FCSTD DOCUMENT  (FreeCAD 0.19R)
Label: cebelnjak
License: All rights reserved
LicenseURL: http://en.wikipedia.org/wiki/All_rights_reserved
objects: App::Link×5, App::DocumentObjectGroup×3, PartDesign::CoordinateSystem×1, App::FeaturePython×1, App::Part×1, TechDraw::DrawSVGTemplate×1, TechDraw::DrawViewPart×1, TechDraw::DrawPage×1
note: 1 computed .brp shape members not serialized (recipe doc carries the construction recipe); baked Part::Feature solids carry a one-line shape summary decoded from their .brp
EXTERNAL_REF file=podstavek.FCStd obj=LCS_Origin
EXTERNAL_REF file=podstavek.FCStd obj=Assembly
EXTERNAL_REF file=panj.FCStd obj=LCS_Origin
EXTERNAL_REF file=podstavek.FCStd obj=LCS_panj1
EXTERNAL_REF file=panj.FCStd obj=Assembly
EXTERNAL_REF file=podstavek.FCStd obj=LCS_panj2
EXTERNAL_REF file=podstavek.FCStd obj=LCS_panj3
EXTERNAL_REF file=podstavek.FCStd obj=LCS_panj4

FEATURE [App::DocumentObjectGroup] Parts
FEATURE [PartDesign::CoordinateSystem] LCS_Origin
  AttacherType = Attacher::AttachEngine3D
  MapMode = 2
  Support = -> [X_Axis]
FEATURE [App::FeaturePython] Variables  # WARN: FeaturePython — macro-defined, semantics opaque (R4)
  Type = App::PropertyContainer
FEATURE [App::DocumentObjectGroup] Constraints
FEATURE [App::DocumentObjectGroup] Configurations
FEATURE [App::Link] podstavek
  AttachedBy = #LCS_Origin
  AttachedTo = Parent Assembly#LCS_Origin
  LinkedObject = -> <external podstavek.FCStd>#Assembly
  SolverId = Asm4EE
  expr: Placement = LCS_Origin.Placement * AttachmentOffset * podstavek#LCS_Origin.Placement ^ -1
FEATURE [App::Link] panj  label="panj_1"
  AttachedBy = #LCS_Origin
  AttachedTo = podstavek#LCS_panj1
  LinkPlacement = pos=(-900,0,500) rot=(0,0,1;0rad)
  LinkedObject = -> <external panj.FCStd>#Assembly
  Placement = pos=(-900,0,500) rot=(0,0,1;0rad)
  SolverId = Asm4EE
  expr: Placement = podstavek.Placement * podstavek#LCS_panj1.Placement * AttachmentOffset * panj#LCS_Origin.Placement ^ -1
FEATURE [App::Link] panj_2
  AttachedBy = #LCS_Origin
  AttachedTo = podstavek#LCS_panj2
  LinkPlacement = pos=(-300,0,500) rot=(0,0,1;0rad)
  LinkedObject = -> <external panj.FCStd>#Assembly
  Placement = pos=(-300,0,500) rot=(0,0,1;0rad)
  SolverId = Asm4EE
  expr: Placement = podstavek.Placement * podstavek#LCS_panj2.Placement * AttachmentOffset * panj#LCS_Origin.Placement ^ -1
FEATURE [App::Link] panj_3
  AttachedBy = #LCS_Origin
  AttachedTo = podstavek#LCS_panj3
  LinkPlacement = pos=(300,0,500) rot=(0,0,1;0rad)
  LinkedObject = -> <external panj.FCStd>#Assembly
  Placement = pos=(300,0,500) rot=(0,0,1;0rad)
  SolverId = Asm4EE
  expr: Placement = podstavek.Placement * podstavek#LCS_panj3.Placement * AttachmentOffset * panj#LCS_Origin.Placement ^ -1
FEATURE [App::Link] panj_4
  AttachedBy = #LCS_Origin
  AttachedTo = podstavek#LCS_panj4
  LinkPlacement = pos=(900,0,500) rot=(0,0,1;0rad)
  LinkedObject = -> <external panj.FCStd>#Assembly
  Placement = pos=(900,0,500) rot=(0,0,1;0rad)
  SolverId = Asm4EE
  expr: Placement = podstavek.Placement * podstavek#LCS_panj4.Placement * AttachmentOffset * panj#LCS_Origin.Placement ^ -1
FEATURE [App::Part] Assembly
  AssemblyType = Part::Link
  Group = -> [LCS_Origin,Variables,Constraints,Configurations,podstavek,panj,panj_2,panj_3,panj_4]
  Origin = -> Origin
  Type = Assembly
FEATURE [TechDraw::DrawSVGTemplate] Template
  EditableTexts = AVTOR=Brane Borštnik; AVTOR_2=Risal: Janez Paternoster; DATUM=6.5.2022; MERILO=1:10; NAZIV=Dadant-Blatt panji; STRAN=Stran 1/1; VIR=https://github.com/<owner>/Dadant-Blatt
  Height = 210
  Orientation = 1
  Width = 297
FEATURE [TechDraw::DrawViewPart] View
  CoarseView = false
  Direction = (0.333,-0.882,0.333)
  Focus = 100
  HardHidden = false
  IsoCount = 0
  IsoHidden = false
  IsoVisible = false
  LockPosition = false
  Perspective = false
  Rotation = 0
  Scale = 0.09
  ScaleType = 0
  SeamHidden = false
  SeamVisible = true
  SmoothHidden = false
  SmoothVisible = true
  Source = -> [Assembly]
  X = 148.5
  XDirection = (0.935,0.354,0)
  Y = 105
FEATURE [TechDraw::DrawPage] Page
  KeepUpdated = true
  NextBalloonIndex = 1
  ProjectionType = 0
  Scale = 0.09
  Template = -> Template
  Views = -> [View]

RESOLVED EXTERNAL PARTS (link-assembly join: the EXTERNAL_REF files above that resolve inside this repo's crawl, each included once):
---- part panj.FCStd = doc fcstd_6ccb10f4a623 ----
FCSTD DOCUMENT  (FreeCAD 0.19R)
Label: panj
License: All rights reserved
LicenseURL: http://en.wikipedia.org/wiki/All_rights_reserved
objects: App::Link×9, PartDesign::CoordinateSystem×4, App::DocumentObjectGroup×3, TechDraw::DrawSVGTemplate×3, TechDraw::DrawViewPart×3, TechDraw::DrawPage×3, App::Part×2, TechDraw::DrawViewSection×2, App::FeaturePython×1, Sketcher::SketchObject×1, PartDesign::Pad×1, PartDesign::Body×1
note: 8 computed .brp shape members not serialized (recipe doc carries the construction recipe); baked Part::Feature solids carry a one-line shape summary decoded from their .brp
EXTERNAL_REF file=podnica_ohisje.FCStd obj=LCS_bottom
EXTERNAL_REF file=podnica_ohisje.FCStd obj=Assembly
EXTERNAL_REF file=podnica_ohisje.FCStd obj=LCS_insert_low
EXTERNAL_REF file=smukalnik.FCStd obj=LCS_podnica
EXTERNAL_REF file=smukalnik.FCStd obj=Assembly
EXTERNAL_REF file=podnica_ohisje.FCStd obj=LCS_insert
EXTERNAL_REF file=smukalnik_mreza.FCStd obj=LCS_spreaj
EXTERNAL_REF file=smukalnik_mreza.FCStd obj=Assembly
EXTERNAL_REF file=podnica_ohisje.FCStd obj=LCS_pokrovcek
EXTERNAL_REF file=podnica_pokrovcek.FCStd obj=LCS_Origin
EXTERNAL_REF file=podnica_pokrovcek.FCStd obj=Assembly
EXTERNAL_REF file=naklada.FCStd obj=LCS_Origin
EXTERNAL_REF file=podnica_ohisje.FCStd obj=LCS_Origin
EXTERNAL_REF file=naklada.FCStd obj=Assembly
EXTERNAL_REF file=naklada.FCStd obj=LCS_1
EXTERNAL_REF file=naklada_nizka.FCStd obj=LCS_Origin
EXTERNAL_REF file=naklada_nizka.FCStd obj=Assembly
EXTERNAL_REF file=naklada_nizka.FCStd obj=LCS_1
EXTERNAL_REF file=pokrov.FCStd obj=LCS_botton
EXTERNAL_REF file=pokrov.FCStd obj=Assembly
EXTERNAL_REF file=pokrov.FCStd obj=LCS_1
EXTERNAL_REF file=streha.FCStd obj=LCS_Origin
EXTERNAL_REF file=streha.FCStd obj=Assembly

FEATURE [PartDesign::CoordinateSystem] LCS_Origin
  AttacherType = Attacher::AttachEngine3D
  MapMode = 2
  Support = -> [X_Axis]
FEATURE [App::FeaturePython] Variables  # WARN: FeaturePython — macro-defined, semantics opaque (R4)
  Type = App::PropertyContainer
FEATURE [App::DocumentObjectGroup] Constraints
FEATURE [App::DocumentObjectGroup] Configurations
FEATURE [App::Link] podnica_ohisje
  AttachedBy = #LCS_bottom
  AttachedTo = Parent Assembly#LCS_Origin
  LinkPlacement = pos=(0,0,120) rot=(0,0,1;0rad)
  LinkedObject = -> <external podnica_ohisje.FCStd>#Assembly
  Placement = pos=(0,0,120) rot=(0,0,1;0rad)
  SolverId = Asm4EE
  expr: Placement = LCS_Origin.Placement * AttachmentOffset * podnica_ohisje#LCS_bottom.Placement ^ -1
FEATURE [App::Link] smukalnik
  AttachedBy = #LCS_podnica
  AttachedTo = podnica_ohisje#LCS_insert_low
  LinkPlacement = pos=(0,-234,65) rot=(0,0,1;0rad)
  LinkedObject = -> <external smukalnik.FCStd>#Assembly
  Placement = pos=(0,-234,65) rot=(0,0,1;0rad)
  SolverId = Asm4EE
  expr: Placement = podnica_ohisje.Placement * podnica_ohisje#LCS_insert_low.Placement * AttachmentOffset * smukalnik#LCS_podnica.Placement ^ -1
FEATURE [App::Link] smukalnik_mreza
  AttachedBy = #LCS_spreaj
  AttachedTo = podnica_ohisje#LCS_insert
  LinkPlacement = pos=(0,18.5,35) rot=(0,0,1;0rad)
  LinkedObject = -> <external smukalnik_mreza.FCStd>#Assembly
  Placement = pos=(0,18.5,35) rot=(0,0,1;0rad)
  SolverId = Asm4EE
  expr: Placement = podnica_ohisje.Placement * podnica_ohisje#LCS_insert.Placement * AttachmentOffset * smukalnik_mreza#LCS_spreaj.Placement ^ -1
FEATURE [App::Link] podnica_pokrovcek
  AttachedBy = #LCS_Origin
  AttachedTo = podnica_ohisje#LCS_pokrovcek
  LinkPlacement = pos=(0,-252,35) rot=(0,0,1;0rad)
  LinkedObject = -> <external podnica_pokrovcek.FCStd>#Assembly
  Placement = pos=(0,-252,35) rot=(0,0,1;0rad)
  SolverId = Asm4EE
  expr: Placement = podnica_ohisje.Placement * podnica_ohisje#LCS_pokrovcek.Placement * AttachmentOffset * podnica_pokrovcek#LCS_Origin.Placement ^ -1
FEATURE [App::Link] naklada
  AttachedBy = #LCS_Origin
  AttachedTo = podnica_ohisje#LCS_Origin
  LinkPlacement = pos=(0,0,120) rot=(0,0,1;0rad)
  LinkedObject = -> <external naklada.FCStd>#Assembly
  Placement = pos=(0,0,120) rot=(0,0,1;0rad)
  SolverId = Asm4EE
  expr: Placement = podnica_ohisje.Placement * podnica_ohisje#LCS_Origin.Placement * AttachmentOffset * naklada#LCS_Origin.Placement ^ -1
FEATURE [PartDesign::CoordinateSystem] LCS_0  label="LCS_bottom"
  AttacherType = Attacher::AttachEngine3D
  MapMode = 2
  Support = -> [X_Axis001]
FEATURE [PartDesign::CoordinateSystem] LCS_0001
  AttacherType = Attacher::AttachEngine3D
  MapMode = 2
  Support = -> [X_Axis002]
FEATURE [Sketcher::SketchObject] Sketch
  FullyConstrained = true
  MapMode = 5
  Support = -> [XY_Plane002]
  sketch-geometry (4):
    g0: LineSegment StartX=-214 StartY=-249.5 StartZ=0 EndX=214 EndY=-249.5 EndZ=0
    g1: LineSegment StartX=214 StartY=-249.5 StartZ=0 EndX=214 EndY=249.5 EndZ=0
    g2: LineSegment StartX=214 StartY=249.5 StartZ=0 EndX=-214 EndY=249.5 EndZ=0
    g3: LineSegment StartX=-214 StartY=249.5 StartZ=0 EndX=-214 EndY=-249.5 EndZ=0
  constraints (10):
    c: Coincident(g0,g1)
    c: Coincident(g1,g2)
    c: Coincident(g2,g3)
    c: Coincident(g3,g0)
    c: Horizontal(g2)
    c: Vertical(g3)
    c: Symmetric(g0,g0,g-2)
    c: Symmetric(g0,g1,g-1)
    c: DistanceX(g2,g2) = 428
    c: DistanceY(g1,g1) = 499
FEATURE [PartDesign::Pad] Pad
  Direction = (1,1,1)
  Length = 3
  Length2 = 100
  Profile = -> Sketch
  Type = 0
FEATURE [PartDesign::Body] Body
  Group = -> [LCS_0001,Sketch,Pad]
  Origin = -> Origin002
  Tip = -> Pad
FEATURE [PartDesign::CoordinateSystem] LCS_1  label="LCS_up"
  AttacherType = Attacher::AttachEngine3D
  Placement = pos=(0,0,3) rot=(0,0,1;0rad)
FEATURE [App::Part] maticna_resetka
  Group = -> [LCS_0,Body,LCS_1]
  Origin = -> Origin001
FEATURE [App::DocumentObjectGroup] Parts
  Group = -> [maticna_resetka]
FEATURE [App::Link] maticna_resetka001
  AssemblyType = Part::Link
  AttachedBy = #LCS_0
  AttachedTo = naklada#LCS_1
  LinkPlacement = pos=(0,0,420) rot=(0,0,1;0rad)
  LinkedObject = -> maticna_resetka
  Placement = pos=(0,0,420) rot=(0,0,1;0rad)
  SolverId = Asm4EE
  expr: Placement = naklada.Placement * naklada#LCS_1.Placement * AttachmentOffset * LCS_0.Placement ^ -1
FEATURE [App::Link] naklada_nizka
  AttachedBy = #LCS_Origin
  AttachedTo = maticna_resetka001#LCS_1
  LinkPlacement = pos=(0,0,423) rot=(0,0,1;0rad)
  LinkedObject = -> <external naklada_nizka.FCStd>#Assembly
  Placement = pos=(0,0,423) rot=(0,0,1;0rad)
  SolverId = Asm4EE
  expr: Placement = maticna_resetka001.Placement * LCS_1.Placement * AttachmentOffset * naklada_nizka#LCS_Origin.Placement ^ -1
FEATURE [App::Link] pokrov
  AttachedBy = #LCS_botton
  AttachedTo = naklada_nizka#LCS_1
  LinkPlacement = pos=(0,0,641) rot=(0,0,1;0rad)
  LinkedObject = -> <external pokrov.FCStd>#Assembly
  Placement = pos=(0,0,641) rot=(0,0,1;0rad)
  SolverId = Asm4EE
  expr: Placement = naklada_nizka.Placement * naklada_nizka#LCS_1.Placement * AttachmentOffset * pokrov#LCS_botton.Placement ^ -1
FEATURE [App::Link] streha
  AttachedBy = #LCS_Origin
  AttachedTo = pokrov#LCS_1
  LinkPlacement = pos=(0,0,701) rot=(0,0,1;0rad)
  LinkedObject = -> <external streha.FCStd>#Assembly
  Placement = pos=(0,0,701) rot=(0,0,1;0rad)
  SolverId = Asm4EE
  expr: Placement = pokrov.Placement * pokrov#LCS_1.Placement * AttachmentOffset * streha#LCS_Origin.Placement ^ -1
FEATURE [App::Part] Assembly
  AssemblyType = Part::Link
  Group = -> [LCS_Origin,Variables,Constraints,Configurations,podnica_ohisje,smukalnik,smukalnik_mreza,podnica_pokrovcek,naklada,maticna_resetka001,naklada_nizka,pokrov,streha]
  Origin = -> Origin
  Type = Assembly
FEATURE [TechDraw::DrawSVGTemplate] Template
  EditableTexts = AVTOR=Brane Borštnik; AVTOR_2=Risal: Janez Paternoster; DATUM=6.5.2022; MERILO=1:4; NAZIV=Dadant-Blatt panj; STRAN=Stran 1/3; VIR=https://github.com/<owner>/Dadant-Blatt
  Height = 297
  Orientation = 0
  Width = 210
FEATURE [TechDraw::DrawViewPart] View
  CoarseView = false
  Direction = (0.577,-0.577,0.577)
  Focus = 100
  HardHidden = false
  IsoCount = 0
  IsoHidden = false
  IsoVisible = false
  LockPosition = false
  Perspective = false
  Rotation = 0
  Scale = 0.25
  ScaleType = 0
  SeamHidden = false
  SeamVisible = true
  SmoothHidden = false
  SmoothVisible = true
  Source = -> [Assembly]
  X = 112.091
  XDirection = (0.707,0.707,0)
  Y = 158.928
FEATURE [TechDraw::DrawPage] Page  label="Page1"
  KeepUpdated = true
  NextBalloonIndex = 1
  ProjectionType = 0
  Scale = 0.25
  Template = -> Template
  Views = -> [View]
FEATURE [TechDraw::DrawSVGTemplate] Template001
  EditableTexts = AVTOR=Brane Borštnik; AVTOR_2=Risal: Janez Paternoster; DATUM=6.5.2022; MERILO=1:3,33; NAZIV=Dadant-Blatt panj; STRAN=Stran 2/3; VIR=https://github.com/<owner>/Dadant-Blatt
  Height = 297
  Orientation = 0
  Width = 210
FEATURE [TechDraw::DrawViewPart] View002
  CoarseView = false
  Direction = (0,-1,0)
  Focus = 100
  HardHidden = false
  IsoCount = 0
  IsoHidden = false
  IsoVisible = false
  LockPosition = false
  Perspective = false
  Rotation = 0
  Scale = 0.3
  ScaleType = 0
  SeamHidden = false
  SeamVisible = true
  SmoothHidden = false
  SmoothVisible = true
  Source = -> [Assembly]
  X = -84.3792
  XDirection = (1,0,0)
  Y = 158.511
FEATURE [TechDraw::DrawViewSection] SectionView  label="Section  - "
  BaseView = -> View002
  CoarseView = false
  CutSurfaceDisplay = 2
  Direction = (-1,0,0)
  FileGeomPattern = <path>
  FileHatchPattern = <path>
  Focus = 100
  FuseBeforeCut = false
  HardHidden = false
  HatchScale = 1
  IsoCount = 0
  IsoHidden = false
  IsoVisible = false
  LockPosition = false
  NameGeomPattern = Diamant
  Perspective = false
  Rotation = 0
  Scale = 0.3
  ScaleType = 0
  SeamHidden = false
  SeamVisible = true
  SectionDirection = 0
  SectionNormal = (-1,0,0)
  SectionOrigin = (0,-25,359.5)
  SmoothHidden = false
  SmoothVisible = true
  Source = -> [Assembly]
  X = 113.76
  XDirection = (0,-1,0)
  Y = 161.014
FEATURE [TechDraw::DrawPage] Page001  label="Page2"
  KeepUpdated = true
  NextBalloonIndex = 1
  ProjectionType = 0
  Scale = 0.3
  Template = -> Template001
  Views = -> [View002,SectionView]
FEATURE [TechDraw::DrawSVGTemplate] Template002
  EditableTexts = AVTOR=Brane Borštnik; AVTOR_2=Risal: Janez Paternoster; DATUM=6.5.2022; MERILO=1:3,33; NAZIV=Dadant-Blatt panj; STRAN=Stran 3/3; VIR=https://github.com/<owner>/Dadant-Blatt
  Height = 297
  Orientation = 0
  Width = 210
FEATURE [TechDraw::DrawViewPart] View003
  CoarseView = false
  Direction = (1,0,0)
  Focus = 100
  HardHidden = false
  IsoCount = 0
  IsoHidden = false
  IsoVisible = false
  LockPosition = false
  Perspective = false
  Rotation = 0
  Scale = 0.3
  ScaleType = 0
  SeamHidden = false
  SeamVisible = true
  SmoothHidden = false
  SmoothVisible = true
  Source = -> [Assembly]
  X = -108.156
  XDirection = (0,1,0)
  Y = 148.083
FEATURE [TechDraw::DrawViewSection] SectionView001  label="Section  - 001"
  BaseView = -> View003
  CoarseView = false
  CutSurfaceDisplay = 2
  Direction = (0,-1,0)
  FileGeomPattern = <path>
  FileHatchPattern = <path>
  Focus = 100
  FuseBeforeCut = false
  HardHidden = false
  HatchScale = 1
  IsoCount = 0
  IsoHidden = false
  IsoVisible = false
  LockPosition = false
  NameGeomPattern = Diamant
  Perspective = false
  Rotation = 0
  Scale = 0.3
  ScaleType = 0
  SeamHidden = false
  SeamVisible = true
  SectionDirection = 0
  SectionNormal = (0,-1,0)
  SectionOrigin = (0,-25,359.5)
  SmoothHidden = false
  SmoothVisible = true
  Source = -> [Assembly]
  X = 111.674
  XDirection = (1,0,0)
  Y = 160.18
FEATURE [TechDraw::DrawPage] Page002  label="Page3"
  KeepUpdated = true
  NextBalloonIndex = 1
  ProjectionType = 0
  Scale = 0.3
  Template = -> Template002
  Views = -> [View003,SectionView001]
note: 4 file-system paths scrubbed to <path> (originals preserved in the JSON sidecar)
---- part podstavek.FCStd = doc fcstd_0671ba742b50 ----
FCSTD DOCUMENT  (FreeCAD 0.19R)
Label: podstavek
License: All rights reserved
LicenseURL: http://en.wikipedia.org/wiki/All_rights_reserved
objects: PartDesign::CoordinateSystem×12, App::Link×8, TechDraw::DrawViewDimension×8, Sketcher::SketchObject×7, PartDesign::Pad×5, App::Part×4, App::DocumentObjectGroup×3, PartDesign::Body×3, PartDesign::Pocket×2, TechDraw::DrawViewPart×2, App::FeaturePython×1, TechDraw::DrawSVGTemplate×1, TechDraw::DrawViewSection×1, TechDraw::DrawViewAnnotation×1, TechDraw::DrawPage×1
note: 36 computed .brp shape members not serialized (recipe doc carries the construction recipe); baked Part::Feature solids carry a one-line shape summary decoded from their .brp

FEATURE [PartDesign::CoordinateSystem] LCS_Origin
  AttacherType = Attacher::AttachEngine3D
  MapMode = 2
  Support = -> [X_Axis]
FEATURE [App::FeaturePython] Variables  # WARN: FeaturePython — macro-defined, semantics opaque (R4)
  Type = App::PropertyContainer
  beam_thickness = 1.5
  beam_width = 40
  depth = 400
  height = 500
  length = 3000
FEATURE [App::DocumentObjectGroup] Constraints
FEATURE [App::DocumentObjectGroup] Configurations
FEATURE [PartDesign::CoordinateSystem] LCS_0
  AttacherType = Attacher::AttachEngine3D
  MapMode = 2
  Support = -> [X_Axis001]
FEATURE [PartDesign::CoordinateSystem] LCS_0001
  AttacherType = Attacher::AttachEngine3D
  MapMode = 2
  Support = -> [X_Axis002]
FEATURE [Sketcher::SketchObject] Sketch
  FullyConstrained = true
  MapMode = 5
  Placement = pos=(0,0,0) rot=(0.57735,0.57735,0.57735;2.0944rad)
  Support = -> [YZ_Plane002]
  expr: Constraints[27] = Variables.depth / 2
  expr: Constraints[28] = Variables.height
  sketch-geometry (10):
    g0: LineSegment StartX=-160 StartY=460 StartZ=0 EndX=-160 EndY=500 EndZ=0
    g1: LineSegment StartX=-160 StartY=500 StartZ=0 EndX=-200 EndY=500 EndZ=0
    g2: LineSegment StartX=-200 StartY=500 StartZ=0 EndX=-200 EndY=460 EndZ=0
    g3: LineSegment StartX=-200 StartY=460 StartZ=0 EndX=-160 EndY=460 EndZ=0
    g4: Circle CenterX=-180 CenterY=480 CenterZ=0 NormalX=0 NormalY=0 NormalZ=1 AngleXU=0 Radius=28.2843
    g5: LineSegment StartX=-198.5 StartY=461.5 StartZ=0 EndX=-161.5 EndY=461.5 EndZ=0
    g6: LineSegment StartX=-161.5 StartY=461.5 StartZ=0 EndX=-161.5 EndY=498.5 EndZ=0
    g7: LineSegment StartX=-161.5 StartY=498.5 StartZ=0 EndX=-198.5 EndY=498.5 EndZ=0
    g8: LineSegment StartX=-198.5 StartY=498.5 StartZ=0 EndX=-198.5 EndY=461.5 EndZ=0
    g9: Circle CenterX=-180 CenterY=480 CenterZ=0 NormalX=0 NormalY=0 NormalZ=1 AngleXU=0 Radius=26.163
  constraints (29):
    c: Coincident(g0,g1)
    c: Coincident(g1,g2)
    c: Coincident(g2,g3)
    c: Coincident(g3,g0)
    c: Equal(g0,g1)
    c: Equal(g0,g2)
    c: Equal(g0,g3)
    c: PointOnObject(g0,g4)
    c: PointOnObject(g1,g4)
    c: PointOnObject(g2,g4)
    c: PointOnObject(g3,g4)
    c: Coincident(g5,g6)
    c: Coincident(g6,g7)
    c: Coincident(g7,g8)
    c: Coincident(g8,g5)
    c: Equal(g5,g6)
    c: Equal(g5,g7)
    c: Equal(g5,g8)
    c: PointOnObject(g5,g9)
    c: PointOnObject(g6,g9)
    c: PointOnObject(g7,g9)
    c: PointOnObject(g8,g9)
    c: Coincident(g9,g4)
    c: Horizontal(g3)
    c: Horizontal(g5)
    c: DistanceY(g0,g5) = 1.5  's'
    c: DistanceY(g0,g0) = 40
    c: DistanceX(g2,g-1) = 200
    c: DistanceY(g-1,g1) = 500
FEATURE [PartDesign::Pad] Pad
  Direction = (1,1,1)
  Length = 3000
  Length2 = 100
  Midplane = true
  Placement = pos=(0,0,0) rot=(0.57735,0.57735,0.57735;2.0944rad)
  Profile = -> Sketch
  Type = 0
  expr: Length = Variables.length
FEATURE [Sketcher::SketchObject] Sketch001
  ExternalGeometry = -> [Pad]
  FullyConstrained = true
  MapMode = 5
  Support = -> [XY_Plane002]
  sketch-geometry (6):
    g0: LineSegment StartX=-1500 StartY=-200 StartZ=0 EndX=-1460 EndY=-160 EndZ=0
    g1: LineSegment StartX=-1460 StartY=-160 StartZ=0 EndX=-1500 EndY=-160 EndZ=0
    g2: LineSegment StartX=-1500 StartY=-160 StartZ=0 EndX=-1500 EndY=-200 EndZ=0
    g3: LineSegment StartX=1500 StartY=-160 StartZ=0 EndX=1500 EndY=-200 EndZ=0
    g4: LineSegment StartX=1500 StartY=-160 StartZ=0 EndX=1460 EndY=-160 EndZ=0
    g5: LineSegment StartX=1460 StartY=-160 StartZ=0 EndX=1500 EndY=-200 EndZ=0
  constraints (14):
    c: Coincident(g0,g1)
    c: Horizontal(g1)
    c: Coincident(g1,g2)
    c: Equal(g2,g1)
    c: Coincident(g1,g-3)
    c: Coincident(g0,g2)
    c: Coincident(g0,g-3)
    c: Coincident(g3,g4)
    c: Horizontal(g4)
    c: Coincident(g4,g5)
    c: Coincident(g5,g3)
    c: Equal(g3,g4)
    c: Coincident(g3,g-4)
    c: Coincident(g3,g-4)
FEATURE [PartDesign::Pocket] Pocket
  BaseFeature = -> Pad
  Length = 5
  Length2 = 100
  Placement = pos=(0,0,0) rot=(0.57735,0.57735,0.57735;2.0944rad)
  Profile = -> Sketch001
  Reversed = true
  Type = 1
FEATURE [PartDesign::Body] Body
  Group = -> [LCS_0001,Sketch,Pad,Sketch001,Pocket]
  Origin = -> Origin002
  Tip = -> Pocket
FEATURE [App::Part] frame  label="frame_beam_1"
  Group = -> [LCS_0,Body]
  Origin = -> Origin001
FEATURE [PartDesign::CoordinateSystem] LCS_0002
  AttacherType = Attacher::AttachEngine3D
  MapMode = 2
  Support = -> [X_Axis003]
FEATURE [PartDesign::CoordinateSystem] LCS_0003
  AttacherType = Attacher::AttachEngine3D
  MapMode = 2
  Support = -> [X_Axis004]
FEATURE [Sketcher::SketchObject] Sketch002
  FullyConstrained = true
  MapMode = 5
  Placement = pos=(0,0,0) rot=(1,0,0;1.5708rad)
  Support = -> [XZ_Plane004]
  expr: Constraints[25] = Variables.beam_thickness
  expr: Constraints[28] = Variables.length / 2
  expr: Constraints[26] = Variables.beam_width
  expr: Constraints[27] = Variables.height
  sketch-geometry (10):
    g0: LineSegment StartX=1500 StartY=500 StartZ=0 EndX=1460 EndY=500 EndZ=0
    g1: LineSegment StartX=1460 StartY=500 StartZ=0 EndX=1460 EndY=460 EndZ=0
    g2: LineSegment StartX=1460 StartY=460 StartZ=0 EndX=1500 EndY=460 EndZ=0
    g3: LineSegment StartX=1500 StartY=460 StartZ=0 EndX=1500 EndY=500 EndZ=0
    g4: Circle CenterX=1480 CenterY=480 CenterZ=0 NormalX=0 NormalY=0 NormalZ=1 AngleXU=0 Radius=28.2843
    g5: LineSegment StartX=1498.5 StartY=498.5 StartZ=0 EndX=1461.5 EndY=498.5 EndZ=0
    g6: LineSegment StartX=1461.5 StartY=498.5 StartZ=0 EndX=1461.5 EndY=461.5 EndZ=0
    g7: LineSegment StartX=1461.5 StartY=461.5 StartZ=0 EndX=1498.5 EndY=461.5 EndZ=0
    g8: LineSegment StartX=1498.5 StartY=461.5 StartZ=0 EndX=1498.5 EndY=498.5 EndZ=0
    g9: Circle CenterX=1480 CenterY=480 CenterZ=0 NormalX=0 NormalY=0 NormalZ=1 AngleXU=0 Radius=26.163
  constraints (29):
    c: Coincident(g0,g1)
    c: Coincident(g1,g2)
    c: Coincident(g2,g3)
    c: Coincident(g3,g0)
    c: Equal(g0,g1)
    c: Equal(g0,g2)
    c: Equal(g0,g3)
    c: PointOnObject(g0,g4)
    c: PointOnObject(g1,g4)
    c: PointOnObject(g2,g4)
    c: PointOnObject(g3,g4)
    c: Coincident(g5,g6)
    c: Coincident(g6,g7)
    c: Coincident(g7,g8)
    c: Coincident(g8,g5)
    c: Equal(g5,g6)
    c: Equal(g5,g7)
    c: Equal(g5,g8)
    c: PointOnObject(g5,g9)
    c: PointOnObject(g6,g9)
    c: PointOnObject(g7,g9)
    c: PointOnObject(g8,g9)
    c: Coincident(g9,g4)
    c: Horizontal(g7)
    c: Horizontal(g2)
    c: DistanceY(g2,g7) = 1.5
    c: DistanceY(g3,g3) = 40
    c: DistanceY(g-1,g0) = 500
    c: DistanceX(g-1,g2) = 1500
FEATURE [PartDesign::Pad] Pad001
  Direction = (1,1,1)
  Length = 400
  Length2 = 100
  Midplane = true
  Placement = pos=(0,0,0) rot=(1,0,0;1.5708rad)
  Profile = -> Sketch002
  Type = 0
  expr: Length = Variables.depth
FEATURE [Sketcher::SketchObject] Sketch003
  ExternalGeometry = -> [Pad001]
  FullyConstrained = true
  MapMode = 5
  Support = -> [XY_Plane004]
  sketch-geometry (6):
    g0: LineSegment StartX=1460 StartY=200 StartZ=0 EndX=1500 EndY=200 EndZ=0
    g1: LineSegment StartX=1500 StartY=200 StartZ=0 EndX=1460 EndY=160 EndZ=0
    g2: LineSegment StartX=1460 StartY=160 StartZ=0 EndX=1460 EndY=200 EndZ=0
    g3: LineSegment StartX=1460 StartY=-200 StartZ=0 EndX=1460 EndY=-160 EndZ=0
    g4: LineSegment StartX=1460 StartY=-160 StartZ=0 EndX=1500 EndY=-200 EndZ=0
    g5: LineSegment StartX=1500 StartY=-200 StartZ=0 EndX=1460 EndY=-200 EndZ=0
  constraints (14):
    c: Coincident(g0,g1)
    c: Coincident(g1,g2)
    c: Coincident(g2,g0)
    c: Vertical(g3)
    c: Coincident(g3,g4)
    c: Coincident(g4,g5)
    c: Coincident(g5,g3)
    c: Vertical(g2)
    c: Equal(g2,g0)
    c: Equal(g3,g5)
    c: Coincident(g3,g-4)
    c: Coincident(g4,g-4)
    c: Coincident(g0,g-3)
    c: Coincident(g0,g-3)
FEATURE [PartDesign::Pocket] Pocket001
  BaseFeature = -> Pad001
  Length = 5
  Length2 = 100
  Placement = pos=(0,0,0) rot=(1,0,0;1.5708rad)
  Profile = -> Sketch003
  Reversed = true
  Type = 1
FEATURE [PartDesign::Body] Body_2
  Group = -> [LCS_0003,Sketch002,Pad001,Sketch003,Pocket001]
  Origin = -> Origin004
  Tip = -> Pocket001
FEATURE [App::Part] frame_beam_2
  Group = -> [LCS_0002,Body_2]
  Origin = -> Origin003
FEATURE [App::Link] frame_beam_1  label="frame_beam_front"
  AssemblyType = Part::Link
  AttachedBy = #LCS_0
  AttachedTo = Parent Assembly#LCS_Origin
  LinkedObject = -> frame
  SolverId = Asm4EE
  expr: Placement = LCS_Origin.Placement * AttachmentOffset * LCS_0.Placement ^ -1
FEATURE [App::Link] frame_beam  label="frame_beam_rear"
  AssemblyType = Part::Link
  AttachedBy = #LCS_0
  AttachedTo = Parent Assembly#LCS_Origin
  AttachmentOffset = pos=(0,0,0) rot=(0,0,1;3.14159rad)
  LinkPlacement = pos=(0,0,0) rot=(0,0,1;3.14159rad)
  LinkedObject = -> frame
  Placement = pos=(0,0,0) rot=(0,0,1;3.14159rad)
  SolverId = Asm4EE
  expr: Placement = LCS_Origin.Placement * AttachmentOffset * LCS_0.Placement ^ -1
FEATURE [App::Link] frame_beam_2001  label="frame_beam_right"
  AssemblyType = Part::Link
  AttachedBy = #LCS_0002
  AttachedTo = Parent Assembly#LCS_Origin
  LinkedObject = -> frame_beam_2
  SolverId = Asm4EE
  expr: Placement = LCS_Origin.Placement * AttachmentOffset * LCS_0002.Placement ^ -1
FEATURE [App::Link] frame_beam_3  label="frame_beam_left"
  AssemblyType = Part::Link
  AttachedBy = #LCS_0002
  AttachedTo = Parent Assembly#LCS_Origin
  AttachmentOffset = pos=(0,0,0) rot=(0,0,1;3.14159rad)
  LinkPlacement = pos=(0,0,0) rot=(0,0,1;3.14159rad)
  LinkedObject = -> frame_beam_2
  Placement = pos=(0,0,0) rot=(0,0,1;3.14159rad)
  SolverId = Asm4EE
  expr: Placement = LCS_Origin.Placement * AttachmentOffset * LCS_0002.Placement ^ -1
FEATURE [PartDesign::CoordinateSystem] LCS_0004
  AttacherType = Attacher::AttachEngine3D
  MapMode = 2
  Support = -> [X_Axis005]
FEATURE [PartDesign::CoordinateSystem] LCS_0005
  AttacherType = Attacher::AttachEngine3D
  MapMode = 2
  Support = -> [X_Axis006]
FEATURE [Sketcher::SketchObject] Sketch004
  FullyConstrained = true
  MapMode = 5
  Support = -> [XY_Plane006]
  expr: Constraints[14] = (Variables.depth - Variables.beam_width) / 2
  expr: Constraints[13] = Variables.length / 3
  sketch-geometry (5):
    g0: LineSegment StartX=-950 StartY=-130 StartZ=0 EndX=-1050 EndY=-130 EndZ=0
    g1: LineSegment StartX=-1050 StartY=-130 StartZ=0 EndX=-1050 EndY=-230 EndZ=0
    g2: LineSegment StartX=-1050 StartY=-230 StartZ=0 EndX=-950 EndY=-230 EndZ=0
    g3: LineSegment StartX=-950 StartY=-230 StartZ=0 EndX=-950 EndY=-130 EndZ=0
    g4: Circle CenterX=-1000 CenterY=-180 CenterZ=0 NormalX=0 NormalY=0 NormalZ=1 AngleXU=0 Radius=70.7107
  constraints (15):
    c: Coincident(g0,g1)
    c: Coincident(g1,g2)
    c: Coincident(g2,g3)
    c: Coincident(g3,g0)
    c: Equal(g0,g1)
    c: Equal(g0,g2)
    c: Equal(g0,g3)
    c: PointOnObject(g0,g4)
    c: PointOnObject(g1,g4)
    c: PointOnObject(g2,g4)
    c: PointOnObject(g3,g4)
    c: Horizontal(g2)
    c: DistanceX(g2,g2) = 100
    c: DistanceX(g4,g-1) = 1000
    c: DistanceY(g4,g-1) = 180
FEATURE [PartDesign::Pad] Pad002
  Direction = (1,1,1)
  Length = 2
  Length2 = 100
  Profile = -> Sketch004
  Type = 0
FEATURE [Sketcher::SketchObject] Sketch005
  ExternalGeometry = -> [Pad002]
  FullyConstrained = true
  MapMode = 5
  Placement = pos=(0,0,2) rot=(0,0,1;0rad)
  Support = -> [Pad002,XY_Plane]
  expr: Constraints[30] = Variables.beam_thickness
  expr: Constraints[29] = Variables.beam_width
  sketch-geometry (11):
    g0: LineSegment StartX=-980 StartY=-160 StartZ=0 EndX=-1020 EndY=-160 EndZ=0
    g1: LineSegment StartX=-1020 StartY=-160 StartZ=0 EndX=-1020 EndY=-200 EndZ=0
    g2: LineSegment StartX=-1020 StartY=-200 StartZ=0 EndX=-980 EndY=-200 EndZ=0
    g3: LineSegment StartX=-980 StartY=-200 StartZ=0 EndX=-980 EndY=-160 EndZ=0
    g4: Circle CenterX=-1000 CenterY=-180 CenterZ=0 NormalX=0 NormalY=0 NormalZ=1 AngleXU=0 Radius=28.2843
    g5: LineSegment StartX=-981.5 StartY=-161.5 StartZ=0 EndX=-1018.5 EndY=-161.5 EndZ=0
    g6: LineSegment StartX=-1018.5 StartY=-161.5 StartZ=0 EndX=-1018.5 EndY=-198.5 EndZ=0
    g7: LineSegment StartX=-1018.5 StartY=-198.5 StartZ=0 EndX=-981.5 EndY=-198.5 EndZ=0
    g8: LineSegment StartX=-981.5 StartY=-198.5 StartZ=0 EndX=-981.5 EndY=-161.5 EndZ=0
    g9: Circle CenterX=-1000 CenterY=-180 CenterZ=0 NormalX=0 NormalY=0 NormalZ=1 AngleXU=0 Radius=26.163
    g10: Circle CenterX=-1000 CenterY=-180 CenterZ=0 NormalX=0 NormalY=0 NormalZ=1 AngleXU=0 Radius=70.7107
  constraints (31):
    c: Coincident(g0,g1)
    c: Coincident(g1,g2)
    c: Coincident(g2,g3)
    c: Coincident(g3,g0)
    c: Equal(g0,g1)
    c: Equal(g0,g2)
    c: Equal(g0,g3)
    c: PointOnObject(g0,g4)
    c: PointOnObject(g1,g4)
    c: PointOnObject(g2,g4)
    c: PointOnObject(g3,g4)
    c: Coincident(g5,g6)
    c: Coincident(g6,g7)
    c: Coincident(g7,g8)
    c: Coincident(g8,g5)
    c: Equal(g5,g6)
    c: Equal(g5,g7)
    c: Equal(g5,g8)
    c: PointOnObject(g5,g9)
    c: PointOnObject(g6,g9)
    c: PointOnObject(g7,g9)
    c: PointOnObject(g8,g9)
    c: Coincident(g9,g4)
    c: Coincident(g10,g4)
    c: PointOnObject(g-3,g10)
    c: PointOnObject(g-4,g10)
    c: PointOnObject(g-4,g10)
    c: Horizontal(g7)
    c: Horizontal(g2)
    c: DistanceY(g3,g3) = 40
    c: DistanceY(g2,g7) = 1.5
FEATURE [PartDesign::Pad] Pad003
  BaseFeature = -> Pad002
  Direction = (1,1,1)
  Length = 458
  Length2 = 100
  Profile = -> Sketch005
  Type = 0
  expr: Length = Variables.height - Variables.beam_width - 2
FEATURE [Sketcher::SketchObject] Sketch006
  ExternalGeometry = -> [Pad003]
  FullyConstrained = true
  MapMode = 5
  Support = -> [XY_Plane006]
  expr: Constraints[16] = Variables.beam_thickness
  sketch-geometry (10):
    g0: LineSegment StartX=-951.5 StartY=-131.5 StartZ=0 EndX=-1048.5 EndY=-131.5 EndZ=0
    g1: LineSegment StartX=-1048.5 StartY=-131.5 StartZ=0 EndX=-1048.5 EndY=-228.5 EndZ=0
    g2: LineSegment StartX=-1048.5 StartY=-228.5 StartZ=0 EndX=-951.5 EndY=-228.5 EndZ=0
    g3: LineSegment StartX=-951.5 StartY=-228.5 StartZ=0 EndX=-951.5 EndY=-131.5 EndZ=0
    g4: Circle CenterX=-1000 CenterY=-180 CenterZ=0 NormalX=0 NormalY=0 NormalZ=1 AngleXU=0 Radius=68.5894
    g5: Circle CenterX=-1000 CenterY=-180 CenterZ=0 NormalX=0 NormalY=0 NormalZ=1 AngleXU=0 Radius=70.7107
    g6: LineSegment StartX=-1050 StartY=-130 StartZ=0 EndX=-950 EndY=-130 EndZ=0
    g7: LineSegment StartX=-950 StartY=-130 StartZ=0 EndX=-950 EndY=-230 EndZ=0
    g8: LineSegment StartX=-950 StartY=-230 StartZ=0 EndX=-1050 EndY=-230 EndZ=0
    g9: LineSegment StartX=-1050 StartY=-130 StartZ=0 EndX=-1050 EndY=-230 EndZ=0
  constraints (25):
    c: Coincident(g0,g1)
    c: Coincident(g1,g2)
    c: Coincident(g2,g3)
    c: Coincident(g3,g0)
    c: Equal(g0,g1)
    c: Equal(g0,g2)
    c: Equal(g0,g3)
    c: PointOnObject(g0,g4)
    c: PointOnObject(g1,g4)
    c: PointOnObject(g2,g4)
    c: PointOnObject(g3,g4)
    c: Horizontal(g2)
    c: Coincident(g5,g4)
    c: PointOnObject(g-5,g5)
    c: PointOnObject(g-4,g5)
    c: PointOnObject(g-6,g5)
    c: DistanceY(g0,g-5) = 1.5
    c: Coincident(g-4,g6)
    c: Coincident(g6,g-5)
    c: Coincident(g6,g7)
    c: Coincident(g7,g-6)
    c: Coincident(g7,g8)
    c: Coincident(g8,g-6)
    c: Coincident(g9,g6)
    c: Coincident(g9,g8)
FEATURE [PartDesign::Pad] Pad004
  BaseFeature = -> Pad003
  Direction = (1,1,1)
  Length = 100
  Length2 = 100
  Profile = -> Sketch006
  Type = 0
FEATURE [PartDesign::Body] Body_3
  Group = -> [LCS_0005,Sketch004,Pad002,Sketch005,Pad003,Sketch006,Pad004]
  Origin = -> Origin006
  Tip = -> Pad004
FEATURE [PartDesign::CoordinateSystem] LCS_1
  AttacherType = Attacher::AttachEngine3D
  Placement = pos=(-2000,0,0) rot=(0,0,1;0rad)
  expr: .Placement.Base.x = -(Variables.length / 3 * 2)
FEATURE [App::Part] leg
  Group = -> [LCS_0004,Body_3,LCS_1]
  Origin = -> Origin005
FEATURE [App::DocumentObjectGroup] Parts
  Group = -> [frame,frame_beam_2,leg]
FEATURE [App::Link] leg001  label="leg_1"
  AssemblyType = Part::Link
  AttachedBy = #LCS_0004
  AttachedTo = Parent Assembly#LCS_Origin
  LinkedObject = -> leg
  SolverId = Asm4EE
  expr: Placement = LCS_Origin.Placement * AttachmentOffset * LCS_0004.Placement ^ -1
FEATURE [App::Link] leg_2
  AssemblyType = Part::Link
  AttachedBy = #LCS_1
  AttachedTo = Parent Assembly#LCS_Origin
  LinkPlacement = pos=(2000,0,0) rot=(0,0,1;0rad)
  LinkedObject = -> leg
  Placement = pos=(2000,0,0) rot=(0,0,1;0rad)
  SolverId = Asm4EE
  expr: Placement = LCS_Origin.Placement * AttachmentOffset * LCS_1.Placement ^ -1
FEATURE [App::Link] leg_3
  AssemblyType = Part::Link
  AttachedBy = #LCS_0004
  AttachedTo = Parent Assembly#LCS_Origin
  AttachmentOffset = pos=(0,0,0) rot=(0,0,1;3.14159rad)
  LinkPlacement = pos=(0,0,0) rot=(0,0,1;3.14159rad)
  LinkedObject = -> leg
  Placement = pos=(0,0,0) rot=(0,0,1;3.14159rad)
  SolverId = Asm4EE
  expr: Placement = LCS_Origin.Placement * AttachmentOffset * LCS_0004.Placement ^ -1
FEATURE [App::Link] leg_4
  AssemblyType = Part::Link
  AttachedBy = #LCS_1
  AttachedTo = Parent Assembly#LCS_Origin
  AttachmentOffset = pos=(0,0,0) rot=(0,0,1;3.14159rad)
  LinkPlacement = pos=(-2000,2.449e-13,0) rot=(0,0,1;3.14159rad)
  LinkedObject = -> leg
  Placement = pos=(-2000,2.449e-13,0) rot=(0,0,1;3.14159rad)
  SolverId = Asm4EE
  expr: Placement = LCS_Origin.Placement * AttachmentOffset * LCS_1.Placement ^ -1
FEATURE [TechDraw::DrawSVGTemplate] Template
  EditableTexts = AVTOR=Brane Borštnik; AVTOR_2=Risal: Janez Paternoster; DATUM=6.5.2022; MATERIAL=inox; MERILO=1:5; NAZIV=Podstavek; NAZIV_2=Dadant-Blatt panj; STRAN=Stran 1/1; VIR=https://github.com/<owner>/Dadant-Blatt
  Height = 210
  Orientation = 1
  Width = 297
FEATURE [TechDraw::DrawViewPart] View001
  CoarseView = false
  Direction = (0,0,1)
  Focus = 100
  HardHidden = false
  IsoCount = 0
  IsoHidden = false
  IsoVisible = false
  LockPosition = false
  Perspective = false
  Rotation = 0
  Scale = 0.2
  ScaleType = 0
  SeamHidden = false
  SeamVisible = true
  SmoothHidden = false
  SmoothVisible = true
  Source = -> [leg]
  X = 38.9871
  XDirection = (1,0,0)
  Y = 55
FEATURE [TechDraw::DrawViewSection] SectionView  label="Section A - A"
  BaseView = -> View001
  CoarseView = false
  CutSurfaceDisplay = 2
  Direction = (-1,0,0)
  FileGeomPattern = <path>
  FileHatchPattern = <path>
  Focus = 100
  FuseBeforeCut = false
  HardHidden = false
  HatchScale = 1
  IsoCount = 0
  IsoHidden = false
  IsoVisible = false
  LockPosition = false
  NameGeomPattern = Diamant
  Perspective = false
  Rotation = 0
  Scale = 0.2
  ScaleType = 0
  SeamHidden = false
  SeamVisible = true
  SectionDirection = 0
  SectionNormal = (-1,0,0)
  SectionOrigin = (-1000,-180,231)
  SectionSymbol = A
  SmoothHidden = false
  SmoothVisible = true
  Source = -> [leg]
  X = 137.492
  XDirection = (0,0,1)
  Y = 55
FEATURE [TechDraw::DrawViewDimension] Dimension003
  Arbitrary = false
  ArbitraryTolerances = false
  EqualTolerance = true
  FormatSpec = cev ▫%.6g
  FormatSpecOverTolerance = %+.6g
  FormatSpecUnderTolerance = %+.6g
  Inverted = false
  LockPosition = false
  MeasureType = 1
  OverTolerance = 0
  References2D = -> [SectionView]
  Rotation = 0
  Scale = 0.1
  ScaleType = 0
  TheoreticalExact = false
  Type = 2
  UnderTolerance = 0
  X = 61.402
  Y = 16.0323
FEATURE [TechDraw::DrawViewDimension] Dimension004
  Arbitrary = false
  ArbitraryTolerances = false
  EqualTolerance = true
  FormatSpec = cev ▫%.6g
  FormatSpecOverTolerance = %+.6g
  FormatSpecUnderTolerance = %+.6g
  Inverted = false
  LockPosition = false
  MeasureType = 1
  OverTolerance = 0
  References2D = -> [SectionView]
  Rotation = 0
  Scale = 0.1
  ScaleType = 0
  TheoreticalExact = false
  Type = 2
  UnderTolerance = 0
  X = 52.742
  Y = 21.9335
FEATURE [TechDraw::DrawViewDimension] Dimension005
  Arbitrary = false
  ArbitraryTolerances = false
  EqualTolerance = true
  FormatSpec = %.6g
  FormatSpecOverTolerance = %+.6g
  FormatSpecUnderTolerance = %+.6g
  Inverted = false
  LockPosition = false
  MeasureType = 1
  OverTolerance = 0
  References2D = -> [SectionView]
  Rotation = 0
  Scale = 0.1
  ScaleType = 0
  TheoreticalExact = false
  Type = 1
  UnderTolerance = 0
  X = -35.6122
  Y = 25.9891
FEATURE [TechDraw::DrawViewDimension] Dimension006
  Arbitrary = false
  ArbitraryTolerances = false
  EqualTolerance = true
  FormatSpec = %.6g
  FormatSpecOverTolerance = %+.6g
  FormatSpecUnderTolerance = %+.6g
  Inverted = false
  LockPosition = false
  MeasureType = 1
  OverTolerance = 0
  References2D = -> [SectionView]
  Rotation = 0
  Scale = 0.1
  ScaleType = 0
  TheoreticalExact = false
  Type = 1
  UnderTolerance = 0
  X = -1.10007
  Y = 39.0791
FEATURE [TechDraw::DrawViewDimension] Dimension007
  Arbitrary = false
  ArbitraryTolerances = false
  EqualTolerance = true
  FormatSpec = %.6g (ploščica)
  FormatSpecOverTolerance = %+.6g
  FormatSpecUnderTolerance = %+.6g
  Inverted = false
  LockPosition = false
  MeasureType = 1
  OverTolerance = 0
  References2D = -> [SectionView]
  Rotation = 0
  Scale = 0.1
  ScaleType = 0
  TheoreticalExact = false
  Type = 1
  UnderTolerance = 0
  X = -62.8671
  Y = -10.604
FEATURE [TechDraw::DrawViewAnnotation] Annotation
  Font = osifont
  LineSpace = 80
  LockPosition = false
  MaxWidth = -1
  Rotation = 0
  Scale = 0.1
  ScaleType = 0
  Text = Noge imajo bazen\u010dek | proti mravljam, | Napolni se z vodo ali | oljem. Potrebno je | min. 30mm prehoda.
  TextSize = 5
  TextStyle = 0
  X = 250.551
  Y = 52.7949
FEATURE [PartDesign::CoordinateSystem] LCS_panj1
  AttacherType = Attacher::AttachEngine3D
  Placement = pos=(-900,0,500) rot=(0,0,1;0rad)
  expr: .Placement.Base.x = -900
  expr: .Placement.Base.z = Variables.height
FEATURE [PartDesign::CoordinateSystem] LCS_panj2
  AttacherType = Attacher::AttachEngine3D
  Placement = pos=(-300,0,500) rot=(0,0,1;0rad)
  expr: .Placement.Base.z = Variables.height
FEATURE [PartDesign::CoordinateSystem] LCS_panj3
  AttacherType = Attacher::AttachEngine3D
  Placement = pos=(300,0,500) rot=(0,0,1;0rad)
  expr: .Placement.Base.z = Variables.height
FEATURE [PartDesign::CoordinateSystem] LCS_panj4
  AttacherType = Attacher::AttachEngine3D
  Placement = pos=(900,0,500) rot=(0,0,1;0rad)
  expr: .Placement.Base.z = Variables.height
FEATURE [App::Part] Assembly
  AssemblyType = Part::Link
  Group = -> [LCS_Origin,Variables,Constraints,Configurations,frame_beam_1,frame_beam,frame_beam_2001,frame_beam_3,leg001,leg_2,leg_3,leg_4,LCS_panj1,LCS_panj2,LCS_panj3,LCS_panj4]
  Origin = -> Origin
  Type = Assembly
FEATURE [TechDraw::DrawViewPart] View
  CoarseView = false
  Direction = (0.333,-0.882,0.333)
  Focus = 100
  HardHidden = false
  IsoCount = 0
  IsoHidden = false
  IsoVisible = false
  LockPosition = false
  Perspective = false
  Rotation = 0
  Scale = 0.08
  ScaleType = 0
  SeamHidden = false
  SeamVisible = true
  SmoothHidden = false
  SmoothVisible = true
  Source = -> [Assembly]
  X = 141.404
  XDirection = (0.935,0.354,0)
  Y = 137.368
FEATURE [TechDraw::DrawViewDimension] Dimension001
  Arbitrary = false
  ArbitraryTolerances = false
  EqualTolerance = true
  FormatSpec = %.6g
  FormatSpecOverTolerance = %+.6g
  FormatSpecUnderTolerance = %+.6g
  Inverted = false
  LockPosition = false
  MeasureType = 0
  OverTolerance = 0
  References2D = -> [View]
  References3D = -> [Assembly]
  Rotation = 0
  Scale = 0.1
  ScaleType = 0
  TheoreticalExact = false
  Type = 0
  UnderTolerance = 0
  X = -121.286
  Y = 41.4897
FEATURE [TechDraw::DrawViewDimension] Dimension
  Arbitrary = false
  ArbitraryTolerances = false
  EqualTolerance = true
  FormatSpec = %.6g
  FormatSpecOverTolerance = %+.6g
  FormatSpecUnderTolerance = %+.6g
  Inverted = false
  LockPosition = false
  MeasureType = 0
  OverTolerance = 0
  References2D = -> [View]
  References3D = -> [Assembly]
  Rotation = 0
  Scale = 0.1
  ScaleType = 0
  TheoreticalExact = false
  Type = 0
  UnderTolerance = 0
  X = 14.0775
  Y = 35.6315
FEATURE [TechDraw::DrawViewDimension] Dimension002
  Arbitrary = false
  ArbitraryTolerances = false
  EqualTolerance = true
  FormatSpec = %.6g
  FormatSpecOverTolerance = %+.6g
  FormatSpecUnderTolerance = %+.6g
  Inverted = false
  LockPosition = false
  MeasureType = 0
  OverTolerance = 0
  References2D = -> [View]
  References3D = -> [Assembly]
  Rotation = 0
  Scale = 0.1
  ScaleType = 0
  TheoreticalExact = false
  Type = 2
  UnderTolerance = 0
  X = 128.444
  Y = -6.20312
FEATURE [TechDraw::DrawPage] Page
  KeepUpdated = true
  NextBalloonIndex = 1
  ProjectionType = 0
  Scale = 0.1
  Template = -> Template
  Views = -> [View,Dimension001,Dimension,Dimension002,View001,SectionView,Dimension003,Dimension004,Dimension005,Dimension006,Dimension007,Annotation]
note: 2 file-system paths scrubbed to <path> (originals preserved in the JSON sidecar)
